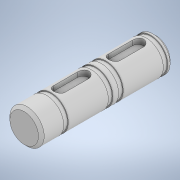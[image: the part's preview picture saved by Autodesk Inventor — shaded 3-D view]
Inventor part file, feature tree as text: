
AUTODESK INVENTOR PART (.ipt)
format: ipt  version: 2020 (Build 240168000, 168)  size: 266,240 bytes
history: native  units: mm
features: projected_geometry x3, revolve x2, sketch x2, plane x1, extrude x1, chamfer x1
ambient origin geometry x8: Origin, YZ Plane, XZ Plane, XY Plane, X Axis, Y Axis, Z Axis, Center Point
bodies: Solid1 (feature_tree)
feature tree (10):
  revolve  "Revolution1"  [1 undecoded]
  revolve  "Revolution2"  Angle=90.0deg
  plane  "Work Plane2"
  extrude  "Extrusion2"  Depth=1.0mm
  chamfer  "Chamfer3"  Distance=0.8mm
  sketch  "Sketch1"  dims[d0=3.0mm d1=23.0mm]
  sketch  "Sketch2"  dims[d2=90.0deg d4=90.0deg d33=2.85mm d34=0.8mm d35=2.85mm d49=6.15mm d50=1.0mm d52=1.0mm d53=0.0mm d54=0.5mm d55=2.0mm d56=45.0deg d57=7.0mm d58=7.0mm d59=1.0mm d60=3.5mm d61=3.5mm d70=0.975mm]
  projected_geometry  "Projected Loop4"
  projected_geometry  "Projected Loop5"
  projected_geometry  "Projected Loop6"
note: 1 required parameter value undecoded (feature->parameter linkage not recoverable at this tier; creation-order binding heuristic only, values carry confidence <= 0.55)
